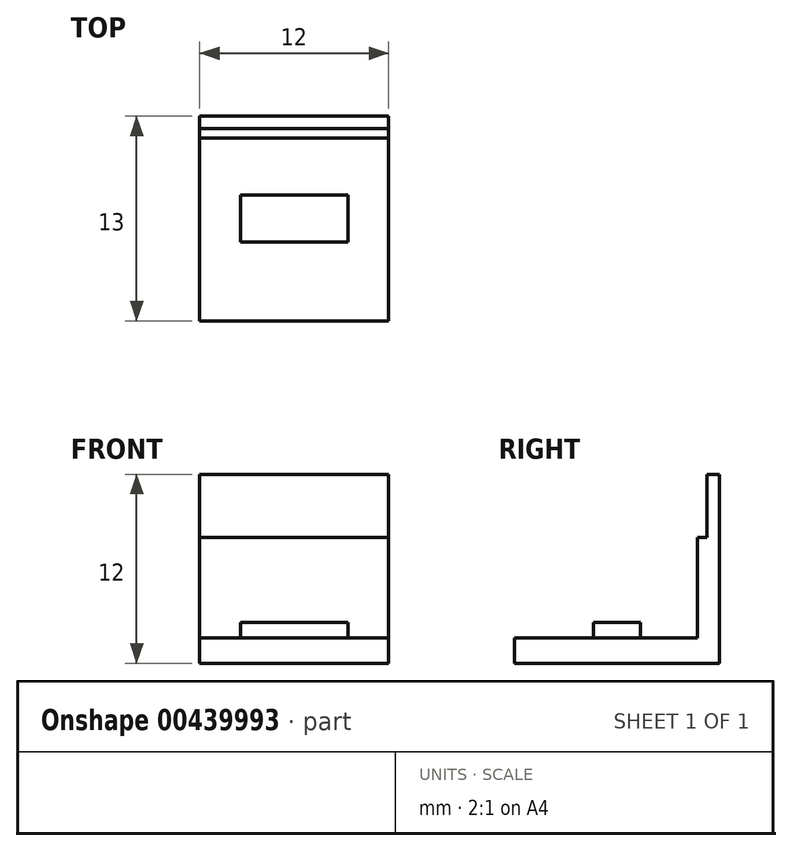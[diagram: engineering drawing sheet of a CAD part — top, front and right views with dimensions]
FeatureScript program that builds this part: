
annotation { "Feature Type Name" : "Feature", "Feature Type Description" : "" }
export const myFeature = defineFeature(function(context is Context, id is Id, definition is map)
    precondition{}
    {
        {
            var Q0;
            Q0=qCreatedBy(makeId("Top.planeOp"),FACE);
            var sketch = newSketch(context, id + "F0", { "sketchPlane" : qUnion([Q0])});
            skLineSegment(sketch, "E0.bottom", {"start": v(0, 0) * mm, "end": v(-12, 0) * mm});
            skLineSegment(sketch, "E0.top", {"start": v(0, 13) * mm, "end": v(-12, 13) * mm});
            skLineSegment(sketch, "E0.left", {"start": v(0, 0) * mm, "end": v(0, 13) * mm});
            skLineSegment(sketch, "E0.right", {"start": v(-12, 0) * mm, "end": v(-12, 13) * mm});
            skLineSegment(sketch, "E1.bottom", {"start": v(-9.4, 8) * mm, "end": v(-2.6, 8) * mm});
            skLineSegment(sketch, "E1.top", {"start": v(-9.4, 5) * mm, "end": v(-2.6, 5) * mm});
            skLineSegment(sketch, "E1.left", {"start": v(-9.4, 8) * mm, "end": v(-9.4, 5) * mm});
            skLineSegment(sketch, "E1.right", {"start": v(-2.6, 8) * mm, "end": v(-2.6, 5) * mm});
            skLineSegment(sketch, "E2", {"start": v(-12, 11.6) * mm, "end": v(0, 11.6) * mm});
            skSolve(sketch);
        }
        {
            var Q0;
            {var subQ0=sQuery(id+"F0.wireOp",EDGE,"E0.top");Q0=makeQuery(id+"F0.imprint","IMPRINT",FACE,{"disambiguationData":[TD([[makeQuery(id+"F0.imprint","IMPRINT",EDGE,{"derivedFrom":subQ0}),1.0]])]});}
            extrude(context, id + "F1", {"entities" : qUnion([Q0]), "depth" : 12 * mm});
        }
        {
            var Q0;
            {var subQ1=sQuery(id+"F0.wireOp",EDGE,"E0.bottom");Q0=makeQuery(id+"F0.imprint","IMPRINT",FACE,{"disambiguationData":[TD([[makeQuery(id+"F0.imprint","IMPRINT",EDGE,{"derivedFrom":subQ1}),-1.0]])]});}
            extrude(context, id + "F2", {"entities" : qUnion([Q0]), "operationType" : NewBodyOperationType.ADD, "depth" : 1.6 * mm});
        }
        {
            var Q0;
            Q0=makeQuery(id+"F0.imprint","IMPRINT",FACE,{"disambiguationData":[TD([[makeQuery(id+"F0.imprint","IMPRINT",EDGE,{"derivedFrom":sQuery(id+"F0.wireOp",EDGE,"E1.bottom")}),-1.0]])]});
            extrude(context, id + "F3", {"entities" : qUnion([Q0]), "operationType" : NewBodyOperationType.ADD, "depth" : 2.6 * mm});
        }
        {
            var Q0;
            Q0=makeQuery(id+"F1.opExtrude","SWEPT_FACE",FACE,{"disambiguationData":[OSD([sQuery(id+"F0.wireOp",EDGE,"E2")])]});
            var sketch = newSketch(context, id + "F4", { "sketchPlane" : qUnion([Q0])});
            skLineSegment(sketch, "E3", {"start": v(0, 8) * mm, "end": v(-12, 8) * mm});
            skLineSegment(sketch, "E4.0.0", {"start": v(-12, 12) * mm, "end": v(-12, 1.6) * mm});
            skLineSegment(sketch, "E4.0.1", {"start": v(-12, 1.6) * mm, "end": v(0, 1.6) * mm});
            skLineSegment(sketch, "E4.0.2", {"start": v(0, 1.6) * mm, "end": v(0, 12) * mm});
            skLineSegment(sketch, "E4.0.3", {"start": v(0, 12) * mm, "end": v(-12, 12) * mm});
            skSolve(sketch);
        }
        {
            var Q0;
            {var subQ0=sQuery(id+"F4.wireOp",EDGE,"E3");Q0=makeQuery(id+"F4.imprint","IMPRINT",FACE,{"disambiguationData":[TD([[makeQuery(id+"F4.imprint","IMPRINT",EDGE,{"derivedFrom":subQ0}),-1.0]])]});}
            extrude(context, id + "F5", {"entities" : qUnion([Q0]), "operationType" : NewBodyOperationType.REMOVE, "oppositeDirection" : true, "depth" : 0.6 * mm});
        }
    });
